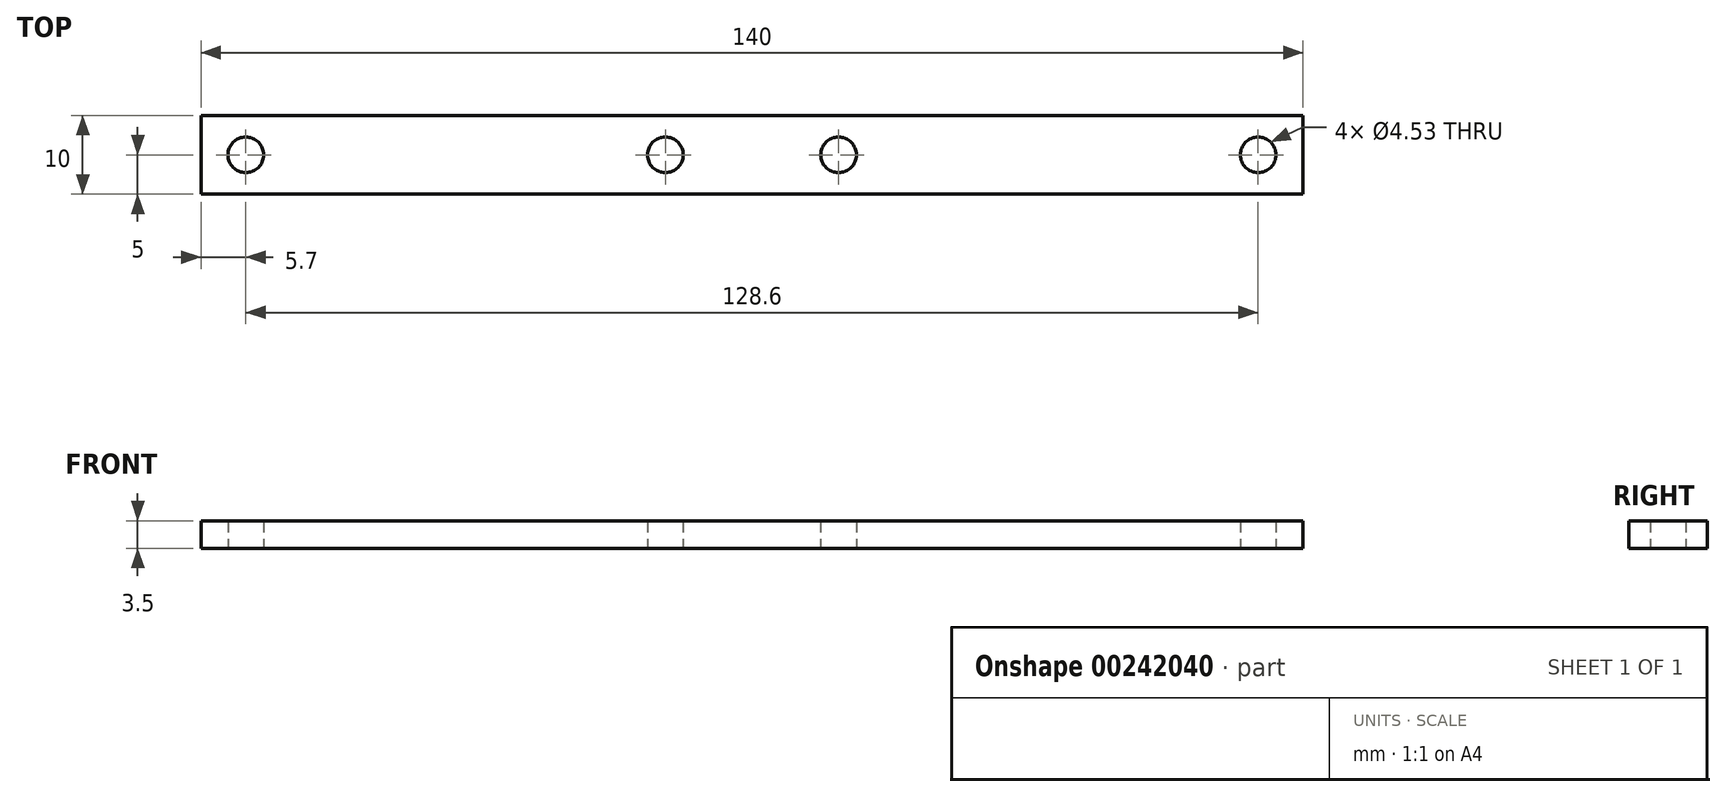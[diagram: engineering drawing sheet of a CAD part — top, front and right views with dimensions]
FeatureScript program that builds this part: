
annotation { "Feature Type Name" : "Feature", "Feature Type Description" : "" }
export const myFeature = defineFeature(function(context is Context, id is Id, definition is map)
    precondition{}
    {
        {
            var Q0;
            Q0=qCreatedBy(makeId("Top.planeOp"),FACE);
            var sketch = newSketch(context, id + "F0", { "sketchPlane" : qUnion([Q0])});
            skLineSegment(sketch, "E0.bottom", {"start": v(0, 0) * mm, "end": v(140, 0) * mm});
            skLineSegment(sketch, "E0.top", {"start": v(0, 10) * mm, "end": v(140, 10) * mm});
            skLineSegment(sketch, "E0.left", {"start": v(0, 0) * mm, "end": v(0, 10) * mm});
            skLineSegment(sketch, "E0.right", {"start": v(140, 0) * mm, "end": v(140, 10) * mm});
            skCircle(sketch, "E1", {"center": v(5.7, 5) * mm, "radius": 2.27 * mm});
            skPoint(sketch, "E2", {"position": v(0, 5) * mm});
            skCircle(sketch, "E3.1.0.0", {"center": v(59, 5) * mm, "radius": 2.27 * mm});
            skLineSegment(sketch, "E3.direction1", {"start": v(5.7, 5) * mm, "end": v(59, 5) * mm, "construction": true});
            skLineSegment(sketch, "E4", {"start": v(70, 10) * mm, "end": v(70, 0) * mm, "construction": true});
            skCircle(sketch, "E5.MirrorC", {"center": v(81, 5) * mm, "radius": 2.27 * mm});
            skCircle(sketch, "E6.MirrorC", {"center": v(134.3, 5) * mm, "radius": 2.27 * mm});
            skSolve(sketch);
        }
        {
            var Q0;
            Q0 = qSketchRegion(id + "F0", true);
            extrude(context, id + "F1", {"entities" : qUnion([Q0]), "depth" : 3.5 * mm});
        }
    });
